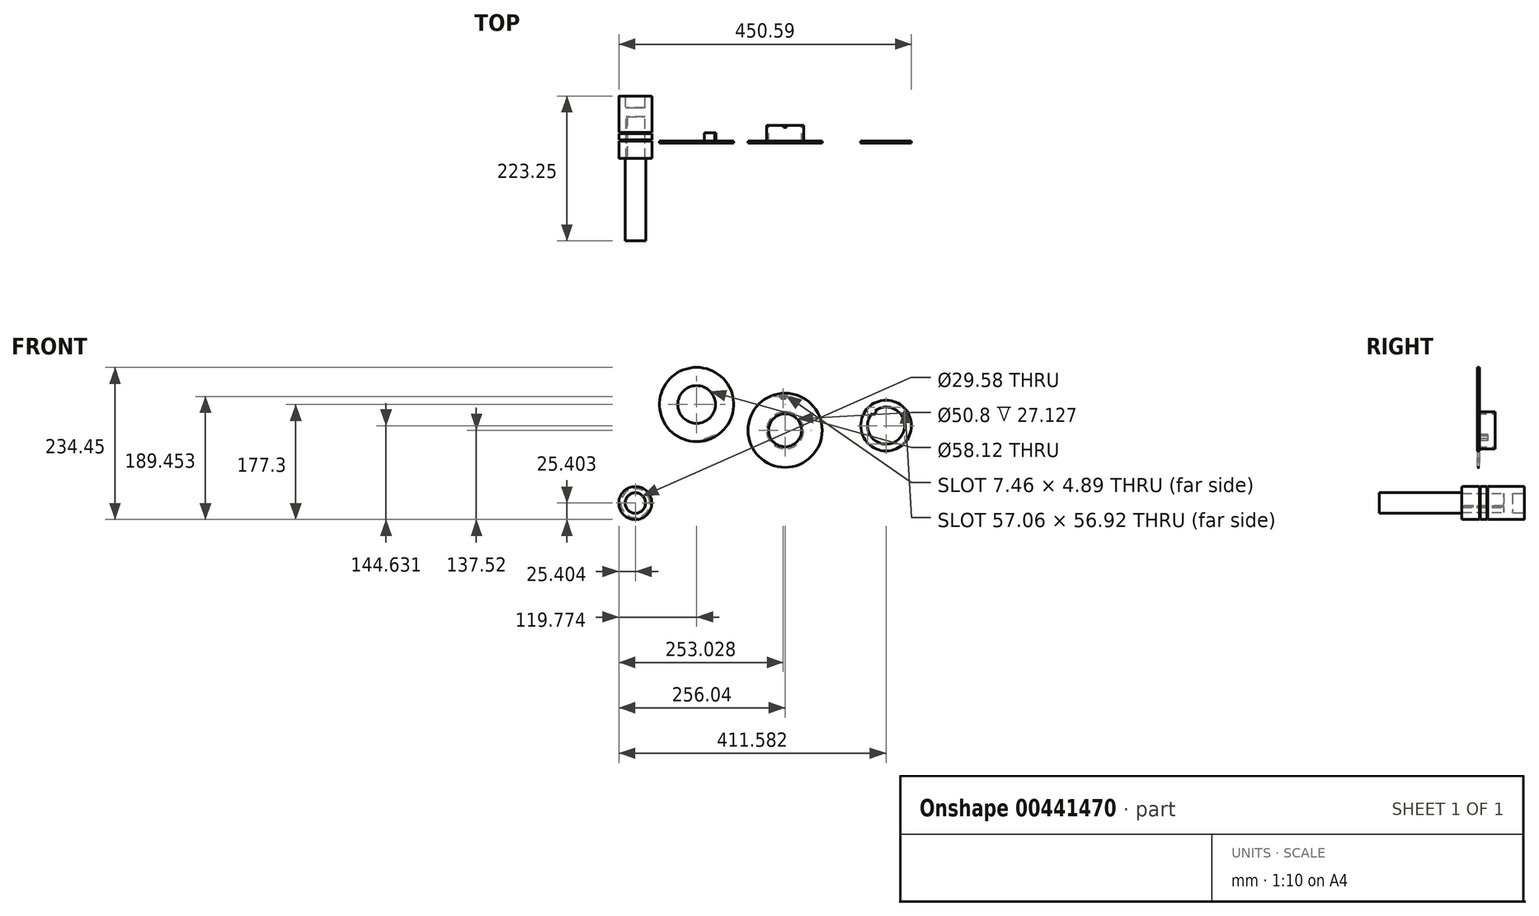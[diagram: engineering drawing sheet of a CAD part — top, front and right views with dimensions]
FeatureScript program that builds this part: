
annotation { "Feature Type Name" : "Feature", "Feature Type Description" : "" }
export const myFeature = defineFeature(function(context is Context, id is Id, definition is map)
    precondition{}
    {
        {
            var Q0;
            Q0=qCreatedBy(makeId("Front.planeOp"),FACE);
            var sketch = newSketch(context, id + "F0", { "sketchPlane" : qUnion([Q0])});
            skCircle(sketch, "E0", {"center": v(0, 0) * mm, "radius": 57.15 * mm});
            skCircle(sketch, "E1", {"center": v(0, 0) * mm, "radius": 25.4 * mm});
            skSolve(sketch);
        }
        {
            var Q0;
            Q0=makeQuery(id+"F0.imprint","IMPRINT",FACE,{"disambiguationData":[TD([[makeQuery(id+"F0.imprint","IMPRINT",EDGE,{"derivedFrom":sQuery(id+"F0.wireOp",EDGE,"E0")}),1.0]])]});
            extrude(context, id + "F1", {"entities" : qUnion([Q0]), "depth" : 3.17 * mm});
        }
        {
            var Q0;
            Q0=makeQuery(id+"F1.opExtrude","CAP_FACE",FACE,{"disambiguationData":[OSD([sQuery(id+"F0.wireOp",EDGE,"E0"),sQuery(id+"F0.wireOp",EDGE,"E1")])],"isStart":false});
            var sketch = newSketch(context, id + "F2", { "sketchPlane" : qUnion([Q0])});
            skLineSegment(sketch, "E2", {"start": v(0.72, 54.09) * mm, "end": v(0.72, 49.8) * mm});
            skLineSegment(sketch, "E3", {"start": v(-6.74, 49.9) * mm, "end": v(-6.62, 54.2) * mm});
            skArc(sketch, "E4", {"start": v(0.72, 54.09) * mm, "mid": v(-2.95, 54.38) * mm, "end": v(-6.62, 54.2) * mm});
            skArc(sketch, "E5", {"start": v(-6.74, 49.9) * mm, "mid": v(-3.02, 49.49) * mm, "end": v(0.72, 49.8) * mm});
            skSolve(sketch);
        }
        {
            var Q0;
            Q0=makeQuery(id+"F2.imprint","IMPRINT",FACE,{"disambiguationData":[TD([[makeQuery(id+"F2.imprint","IMPRINT",EDGE,{"derivedFrom":sQuery(id+"F2.wireOp",EDGE,"E2")}),-1.0]])]});
            extrude(context, id + "F3", {"entities" : qUnion([Q0]), "operationType" : NewBodyOperationType.REMOVE, "oppositeDirection" : true, "depth" : 25.4 * mm});
        }
        {
            var Q0;
            Q0=makeQuery(id+"F1.opExtrude","CAP_FACE",FACE,{"disambiguationData":[OSD([sQuery(id+"F0.wireOp",EDGE,"E0"),sQuery(id+"F0.wireOp",EDGE,"E1")])],"isStart":true});
            var sketch = newSketch(context, id + "F4", { "sketchPlane" : qUnion([Q0])});
            skCircle(sketch, "E6.0", {"center": v(0, 0) * mm, "radius": 25.4 * mm});
            skCircle(sketch, "E7", {"center": v(0, 0) * mm, "radius": 28.58 * mm});
            skSolve(sketch);
        }
        {
            var Q0;
            Q0=makeQuery(id+"F4.imprint","IMPRINT",FACE,{"disambiguationData":[TD([[makeQuery(id+"F4.imprint","IMPRINT",EDGE,{"derivedFrom":sQuery(id+"F4.wireOp",EDGE,"E6.0")}),1.0]])]});
            extrude(context, id + "F5", {"entities" : qUnion([Q0]), "operationType" : NewBodyOperationType.ADD, "depth" : 23.95 * mm});
        }
        {
            var Q0;
            Q0=qCreatedBy(makeId("Top.planeOp"),FACE);
            cPlane(context, id + "F6", {"entities" : qUnion([Q0]), "cplaneType" : CPlaneType.OFFSET, "offset" : 29.72 * mm, "width" : 152.4 * mm, "height" : 152.4 * mm});
        }
        {
            var Q0;
            Q0=qCreatedBy(id+"F6.planeOp",FACE);
            var sketch = newSketch(context, id + "F7", { "sketchPlane" : qUnion([Q0])});
            skLineSegment(sketch, "E8.bottom", {"start": v(-2.43, 24) * mm, "end": v(2.26, 24) * mm});
            skLineSegment(sketch, "E8.top", {"start": v(-2.43, 20.4) * mm, "end": v(2.26, 20.4) * mm});
            skLineSegment(sketch, "E8.left", {"start": v(-2.43, 24) * mm, "end": v(-2.43, 20.4) * mm});
            skLineSegment(sketch, "E8.right", {"start": v(2.26, 24) * mm, "end": v(2.26, 20.4) * mm});
            skSolve(sketch);
        }
        {
            var Q0;
            Q0 = qSketchRegion(id + "F7", true);
            extrude(context, id + "F8", {"entities" : qUnion([Q0]), "operationType" : NewBodyOperationType.REMOVE, "oppositeDirection" : true, "depth" : 25.4 * mm});
        }
        {
            var Q0;
            Q0=qCreatedBy(makeId("Front.planeOp"),FACE);
            var sketch = newSketch(context, id + "F9", { "sketchPlane" : qUnion([Q0])});
            skCircle(sketch, "E9", {"center": v(-136.27, 39.78) * mm, "radius": 57.15 * mm});
            skCircle(sketch, "E10", {"center": v(-136.27, 39.78) * mm, "radius": 29.06 * mm});
            skSolve(sketch);
        }
        {
            var Q0;
            Q0=makeQuery(id+"F9.imprint","IMPRINT",FACE,{"disambiguationData":[TD([[makeQuery(id+"F9.imprint","IMPRINT",EDGE,{"derivedFrom":sQuery(id+"F9.wireOp",EDGE,"E9")}),1.0]])]});
            extrude(context, id + "F10", {"entities" : qUnion([Q0]), "depth" : 3.17 * mm});
        }
        {
            var Q0;
            Q0=makeQuery(id+"F10.opExtrude","CAP_FACE",FACE,{"disambiguationData":[OSD([sQuery(id+"F9.wireOp",EDGE,"E9"),sQuery(id+"F9.wireOp",EDGE,"E10")])],"isStart":true});
            var sketch = newSketch(context, id + "F11", { "sketchPlane" : qUnion([Q0])});
            skPoint(sketch, "E11", {"position": v(123.88, -16.01) * mm});
            skPoint(sketch, "E12", {"position": v(106.52, -9.02) * mm});
            skArc(sketch, "E13", {"start": v(106.52, -9.02) * mm, "mid": v(114.92, -13.2) * mm, "end": v(123.88, -16.01) * mm});
            skArc(sketch, "E14.0", {"start": v(108.2, -6.23) * mm, "mid": v(116.14, -10.2) * mm, "end": v(124.6, -12.84) * mm});
            skLineSegment(sketch, "E15", {"start": v(123.88, -16.01) * mm, "end": v(124.6, -12.84) * mm});
            skLineSegment(sketch, "E16", {"start": v(106.52, -9.02) * mm, "end": v(108.2, -6.23) * mm});
            skSolve(sketch);
        }
        {
            var Q0;
            Q0=makeQuery(id+"F11.imprint","IMPRINT",FACE,{"disambiguationData":[TD([[makeQuery(id+"F11.imprint","IMPRINT",EDGE,{"derivedFrom":sQuery(id+"F11.wireOp",EDGE,"E13")}),1.0]])]});
            extrude(context, id + "F12", {"entities" : qUnion([Q0]), "operationType" : NewBodyOperationType.ADD, "depth" : 12.66 * mm});
        }
        {
            var Q0;
            Q0=qCreatedBy(makeId("Front.planeOp"),FACE);
            var sketch = newSketch(context, id + "F13", { "sketchPlane" : qUnion([Q0])});
            skCircle(sketch, "E17", {"center": v(-230.64, -112.12) * mm, "radius": 25.4 * mm});
            skSolve(sketch);
        }
        {
            var Q0;
            Q0=makeQuery(id+"F13.imprint","IMPRINT",FACE,{"disambiguationData":[TD([[makeQuery(id+"F13.imprint","IMPRINT",EDGE,{"derivedFrom":sQuery(id+"F13.wireOp",EDGE,"E17")}),1.0]])]});
            extrude(context, id + "F14", {"entities" : qUnion([Q0]), "depth" : 26.99 * mm});
        }
        {
            var Q0;
            Q0=makeQuery(id+"F14.opExtrude","CAP_FACE",FACE,{"disambiguationData":[OSD([sQuery(id+"F13.wireOp",EDGE,"E17")])],"isStart":true});
            var sketch = newSketch(context, id + "F15", { "sketchPlane" : qUnion([Q0])});
            skCircle(sketch, "E18", {"center": v(230.64, -112.12) * mm, "radius": 22.23 * mm});
            skSolve(sketch);
        }
        {
            var Q0;
            Q0=makeQuery(id+"F15.imprint","IMPRINT",FACE,{"disambiguationData":[TD([[makeQuery(id+"F15.imprint","IMPRINT",EDGE,{"derivedFrom":sQuery(id+"F15.wireOp",EDGE,"E18")}),1.0]])]});
            extrude(context, id + "F16", {"entities" : qUnion([Q0]), "operationType" : NewBodyOperationType.ADD, "depth" : 1.73 * mm});
        }
        {
            var Q0;
            Q0=makeQuery(id+"F16.opExtrude","CAP_FACE",FACE,{"disambiguationData":[OSD([sQuery(id+"F15.wireOp",EDGE,"E18")])],"isStart":false});
            var sketch = newSketch(context, id + "F17", { "sketchPlane" : qUnion([Q0])});
            skCircle(sketch, "E19.0", {"center": v(230.64, -112.12) * mm, "radius": 25.4 * mm});
            skSolve(sketch);
        }
        {
            var Q0;
            Q0=makeQuery(id+"F17.imprint","IMPRINT",FACE,{"disambiguationData":[TD([[makeQuery(id+"F17.imprint","IMPRINT",EDGE,{"derivedFrom":makeQuery(id+"F16.opExtrude","CAP_EDGE",EDGE,{"disambiguationData":[OSD([sQuery(id+"F15.wireOp",EDGE,"E18")])],"isStart":false})}),1.0]])]});
            var Q1;
            Q1=makeQuery(id+"F17.imprint","IMPRINT",FACE,{"disambiguationData":[TD([[makeQuery(id+"F17.imprint","IMPRINT",EDGE,{"derivedFrom":sQuery(id+"F17.wireOp",EDGE,"E19.0")}),1.0]])]});
            extrude(context, id + "F18", {"entities" : qUnion([Q0, Q1]), "operationType" : NewBodyOperationType.ADD, "depth" : 9.52 * mm});
        }
        {
            var Q0;
            Q0=makeQuery(id+"F18.opExtrude","CAP_FACE",FACE,{"disambiguationData":[OSD([sQuery(id+"F17.wireOp",EDGE,"E19.0")])],"isStart":false});
            var sketch = newSketch(context, id + "F19", { "sketchPlane" : qUnion([Q0])});
            skCircle(sketch, "E20", {"center": v(230.64, -112.12) * mm, "radius": 22.23 * mm});
            skSolve(sketch);
        }
        {
            var Q0;
            Q0=makeQuery(id+"F19.imprint","IMPRINT",FACE,{"disambiguationData":[TD([[makeQuery(id+"F19.imprint","IMPRINT",EDGE,{"derivedFrom":sQuery(id+"F19.wireOp",EDGE,"E20")}),1.0]])]});
            extrude(context, id + "F20", {"entities" : qUnion([Q0]), "operationType" : NewBodyOperationType.ADD, "depth" : 1.73 * mm});
        }
        {
            var Q0;
            Q0=makeQuery(id+"F20.opExtrude","CAP_FACE",FACE,{"disambiguationData":[OSD([sQuery(id+"F19.wireOp",EDGE,"E20")])],"isStart":false});
            var sketch = newSketch(context, id + "F21", { "sketchPlane" : qUnion([Q0])});
            skCircle(sketch, "E21.0", {"center": v(230.64, -112.12) * mm, "radius": 25.4 * mm});
            skSolve(sketch);
        }
        {
            var Q0;
            Q0=makeQuery(id+"F21.imprint","IMPRINT",FACE,{"disambiguationData":[TD([[makeQuery(id+"F21.imprint","IMPRINT",EDGE,{"derivedFrom":makeQuery(id+"F20.opExtrude","CAP_EDGE",EDGE,{"disambiguationData":[OSD([sQuery(id+"F19.wireOp",EDGE,"E20")])],"isStart":false})}),1.0]])]});
            var Q1;
            Q1=makeQuery(id+"F21.imprint","IMPRINT",FACE,{"disambiguationData":[TD([[makeQuery(id+"F21.imprint","IMPRINT",EDGE,{"derivedFrom":sQuery(id+"F21.wireOp",EDGE,"E21.0")}),1.0]])]});
            extrude(context, id + "F22", {"entities" : qUnion([Q0, Q1]), "operationType" : NewBodyOperationType.ADD, "depth" : 56.28 * mm});
        }
        {
            var Q0;
            Q0=makeQuery(id+"F22.opExtrude","CAP_FACE",FACE,{"disambiguationData":[OSD([sQuery(id+"F21.wireOp",EDGE,"E21.0")])],"isStart":false});
            var sketch = newSketch(context, id + "F23", { "sketchPlane" : qUnion([Q0])});
            skCircle(sketch, "E22", {"center": v(230.64, -112.12) * mm, "radius": 14.79 * mm});
            skSolve(sketch);
        }
        {
            var Q0;
            Q0=makeQuery(id+"F23.imprint","IMPRINT",FACE,{"disambiguationData":[TD([[makeQuery(id+"F23.imprint","IMPRINT",EDGE,{"derivedFrom":sQuery(id+"F23.wireOp",EDGE,"E22")}),1.0]])]});
            extrude(context, id + "F24", {"entities" : qUnion([Q0]), "operationType" : NewBodyOperationType.REMOVE, "oppositeDirection" : true, "depth" : 18.4 * mm});
        }
        {
            var Q0;
            Q0=makeQuery(id+"F14.opExtrude","CAP_FACE",FACE,{"disambiguationData":[OSD([sQuery(id+"F13.wireOp",EDGE,"E17")])],"isStart":false});
            var sketch = newSketch(context, id + "F25", { "sketchPlane" : qUnion([Q0])});
            skCircle(sketch, "E23", {"center": v(-230.64, -112.12) * mm, "radius": 15.88 * mm});
            skSolve(sketch);
        }
        {
            var Q0;
            Q0=makeQuery(id+"F25.imprint","IMPRINT",FACE,{"disambiguationData":[TD([[makeQuery(id+"F25.imprint","IMPRINT",EDGE,{"derivedFrom":sQuery(id+"F25.wireOp",EDGE,"E23")}),1.0]])]});
            extrude(context, id + "F26", {"entities" : qUnion([Q0]), "operationType" : NewBodyOperationType.REMOVE, "oppositeDirection" : true, "depth" : 64.36 * mm});
        }
        {
            var Q0;
            Q0=makeQuery(id+"F22.opExtrude","CAP_EDGE",EDGE,{"disambiguationData":[OSD([sQuery(id+"F21.wireOp",EDGE,"E21.0")])],"isStart":false});
            var Q1;
            Q1=makeQuery(id+"F14.opExtrude","CAP_EDGE",EDGE,{"disambiguationData":[OSD([sQuery(id+"F13.wireOp",EDGE,"E17")])],"isStart":false});
            var Q2;
            Q2=makeQuery(id+"F24.boolean.opBoolean","COPY",FACE,{"derivedFrom":makeQuery(id+"F24.opExtrude","CAP_FACE",FACE,{"disambiguationData":[OSD([sQuery(id+"F23.wireOp",EDGE,"E22")])],"isStart":false})});
            var Q3;
            Q3=makeQuery(id+"F24.boolean.opBoolean","COPY",EDGE,{"derivedFrom":makeQuery(id+"F24.opExtrude","CAP_EDGE",EDGE,{"disambiguationData":[OSD([sQuery(id+"F23.wireOp",EDGE,"E22")])],"isStart":true})});
            fillet(context, id + "F27", {"entities" : qUnion([Q0, Q1, Q2, Q3]), "radius" : 1.27 * mm, "tangentPropagation" : true, "allowEdgeOverflow" : false});
        }
        {
            var Q0;
            Q0=makeQuery(id+"F26.boolean.opBoolean","COPY",EDGE,{"derivedFrom":makeQuery(id+"F26.opExtrude","CAP_EDGE",EDGE,{"disambiguationData":[OSD([sQuery(id+"F25.wireOp",EDGE,"E23")])],"isStart":false})});
            chamfer(context, id + "F28", {"entities" : qUnion([Q0]), "width" : 1.27 * mm, "tangentPropagation" : true});
        }
        {
            var Q0;
            Q0=makeQuery(id+"F14.opExtrude","CAP_FACE",FACE,{"disambiguationData":[OSD([sQuery(id+"F13.wireOp",EDGE,"E17")])],"isStart":false});
            var sketch = newSketch(context, id + "F29", { "sketchPlane" : qUnion([Q0])});
            skLineSegment(sketch, "E24", {"start": v(-245.74, -116.99) * mm, "end": v(-243.82, -116.26) * mm});
            skLineSegment(sketch, "E25", {"start": v(-242.98, -118.5) * mm, "end": v(-244.84, -119.2) * mm});
            skArc(sketch, "E26", {"start": v(-242.98, -118.5) * mm, "mid": v(-243.39, -117.37) * mm, "end": v(-243.82, -116.26) * mm});
            skArc(sketch, "E27", {"start": v(-245.74, -116.99) * mm, "mid": v(-245.34, -118.12) * mm, "end": v(-244.84, -119.2) * mm});
            skSolve(sketch);
        }
        {
            var Q0;
            Q0=makeQuery(id+"F29.imprint","IMPRINT",FACE,{"disambiguationData":[TD([[makeQuery(id+"F29.imprint","IMPRINT",EDGE,{"derivedFrom":sQuery(id+"F29.wireOp",EDGE,"E24")}),-1.0]])]});
            var Q1;
            Q1=makeQuery(id+"F26.boolean.opBoolean","COPY",FACE,{"derivedFrom":makeQuery(id+"F26.opExtrude","CAP_FACE",FACE,{"disambiguationData":[OSD([sQuery(id+"F25.wireOp",EDGE,"E23")])],"isStart":false})});
            extrude(context, id + "F30", {"entities" : qUnion([Q0]), "operationType" : NewBodyOperationType.ADD, "endBound" : BoundingType.UP_TO_SURFACE, "oppositeDirection" : true, "endBoundEntityFace" : qUnion([Q1]), "depth" : 25.4 * mm});
        }
        {
            var Q0;
            Q0=makeQuery(id+"F30.opExtrude","CAP_EDGE",EDGE,{"disambiguationData":[OSD([sQuery(id+"F29.wireOp",EDGE,"E26")])],"isStart":true});
            chamfer(context, id + "F31", {"entities" : qUnion([Q0]), "width" : 1.99 * mm, "tangentPropagation" : true});
        }
        {
            var Q0;
            Q0=qCreatedBy(makeId("Front.planeOp"),FACE);
            var sketch = newSketch(context, id + "F32", { "sketchPlane" : qUnion([Q0])});
            skCircle(sketch, "E28", {"center": v(155.57, 7.22) * mm, "radius": 38.99 * mm});
            skCircle(sketch, "E29", {"center": v(155.57, 7.22) * mm, "radius": 28.58 * mm});
            skLineSegment(sketch, "E30", {"start": v(138.7, 30.29) * mm, "end": v(140.88, 27.95) * mm});
            skLineSegment(sketch, "E31", {"start": v(134.02, 26) * mm, "end": v(136.2, 23.66) * mm});
            skArc(sketch, "E32", {"start": v(140.88, 27.95) * mm, "mid": v(138.34, 26.03) * mm, "end": v(136.2, 23.66) * mm});
            skSolve(sketch);
        }
        {
            var Q0;
            Q0 = qSketchRegion(id + "F32", true);
            var Q1;
            {var subQ0=sQuery(id+"F32.wireOp",EDGE,"E30");Q1=makeQuery(id+"F32.imprint","IMPRINT",FACE,{"disambiguationData":[TD([[makeQuery(id+"F32.imprint","IMPRINT",EDGE,{"derivedFrom":subQ0}),-1.0]])]});}
            extrude(context, id + "F33", {"entities" : qUnion([Q0, Q1]), "depth" : 3.17 * mm});
        }
        {
            var Q0;
            Q0=qCreatedBy(makeId("Front.planeOp"),FACE);
            var sketch = newSketch(context, id + "F34", { "sketchPlane" : qUnion([Q0])});
            skCircle(sketch, "E33", {"center": v(271, -56.7) * mm, "radius": 55.3 * mm});
            skSolve(sketch);
        }
        {
            var Q0;
            Q0=makeQuery(id+"F34.imprint","IMPRINT",FACE,{"disambiguationData":[TD([[makeQuery(id+"F34.imprint","IMPRINT",EDGE,{"derivedFrom":sQuery(id+"F34.wireOp",EDGE,"E33")}),1.0]])]});
            extrude(context, id + "F35", {"entities" : qUnion([Q0]), "depth" : 174.5 * mm});
        }
        {
            var Q0;
            Q0=makeQuery(id+"F35.opExtrude","SWEPT_BODY",BODY,{"disambiguationData":[OSD([sQuery(id+"F34.wireOp",EDGE,"E33")])]});
            deleteBodies(context, id + "F36", {"entities" : qUnion([Q0])});
        }
        {
            var Q0;
            Q0=makeQuery(id+"F26.boolean.opBoolean","COPY",FACE,{"derivedFrom":makeQuery(id+"F26.opExtrude","CAP_FACE",FACE,{"disambiguationData":[OSD([sQuery(id+"F25.wireOp",EDGE,"E23")])],"isStart":false})});
            var sketch = newSketch(context, id + "F37", { "sketchPlane" : qUnion([Q0])});
            skCircle(sketch, "E34.0", {"center": v(-230.64, -112.12) * mm, "radius": 24.13 * mm});
            skCircle(sketch, "E35", {"center": v(-230.64, -112.12) * mm, "radius": 15.88 * mm});
            skSolve(sketch);
        }
        {
            var Q0;
            Q0=makeQuery(id+"F37.imprint","IMPRINT",FACE,{"disambiguationData":[TD([[makeQuery(id+"F37.imprint","IMPRINT",EDGE,{"derivedFrom":sQuery(id+"F37.wireOp",EDGE,"E35")}),1.0]])]});
            var Q1;
            {var subQ0=sQuery(id+"F25.wireOp",EDGE,"E23");var subQ1=makeQuery(id+"F26.boolean.opBoolean","COPY",FACE,{"derivedFrom":makeQuery(id+"F26.opExtrude","CAP_FACE",FACE,{"disambiguationData":[OSD([subQ0])],"isStart":false})});var subQ2=subQ1;var subQ17=sQuery(id+"F29.wireOp",EDGE,"E24");var subQ18=makeQuery(id+"F29.imprint","IMPRINT",EDGE,{"derivedFrom":subQ17});Q1=makeQuery(id+"F37.imprint","IMPRINT",FACE,{"disambiguationData":[TD([[makeQuery(id+"F37.imprint","IMPRINT",EDGE,{"derivedFrom":makeQuery(id+"F30.opExtrude","TWEAK_EDGE",EDGE,{"derivedFrom":[subQ2,subQ18]})}),-1.0]])]});}
            var Q2;
            {var subQ0=sQuery(id+"F29.wireOp",EDGE,"E26");var subQ1=sQuery(id+"F29.wireOp",EDGE,"E25");var subQ2=sQuery(id+"F29.wireOp",EDGE,"E24");var subQ3=sQuery(id+"F25.wireOp",EDGE,"E23");Q2=makeQuery(id+"FPU4hDJRsUAHc8M_3.17.F30.boolean.opBoolean","MERGE",FACE,{"derivedFrom":[makeQuery(id+"FPU4hDJRsUAHc8M_3.16.F30.boolean.opBoolean","MERGE",FACE,{"derivedFrom":[makeQuery(id+"FPU4hDJRsUAHc8M_3.15.F30.boolean.opBoolean","MERGE",FACE,{"derivedFrom":[makeQuery(id+"FPU4hDJRsUAHc8M_3.14.F30.boolean.opBoolean","MERGE",FACE,{"derivedFrom":[makeQuery(id+"FPU4hDJRsUAHc8M_3.13.F30.boolean.opBoolean","MERGE",FACE,{"derivedFrom":[makeQuery(id+"FPU4hDJRsUAHc8M_3.12.F30.boolean.opBoolean","MERGE",FACE,{"derivedFrom":[makeQuery(id+"FPU4hDJRsUAHc8M_3.11.F30.boolean.opBoolean","MERGE",FACE,{"derivedFrom":[makeQuery(id+"FPU4hDJRsUAHc8M_3.10.F30.boolean.opBoolean","MERGE",FACE,{"derivedFrom":[makeQuery(id+"FPU4hDJRsUAHc8M_3.9.F30.boolean.opBoolean","MERGE",FACE,{"derivedFrom":[makeQuery(id+"FPU4hDJRsUAHc8M_3.8.F30.boolean.opBoolean","MERGE",FACE,{"derivedFrom":[makeQuery(id+"FPU4hDJRsUAHc8M_3.7.F30.boolean.opBoolean","MERGE",FACE,{"derivedFrom":[makeQuery(id+"FPU4hDJRsUAHc8M_3.6.F30.boolean.opBoolean","MERGE",FACE,{"derivedFrom":[makeQuery(id+"FPU4hDJRsUAHc8M_3.5.F30.boolean.opBoolean","MERGE",FACE,{"derivedFrom":[makeQuery(id+"FPU4hDJRsUAHc8M_3.4.F30.boolean.opBoolean","MERGE",FACE,{"derivedFrom":[makeQuery(id+"FPU4hDJRsUAHc8M_3.3.F30.boolean.opBoolean","MERGE",FACE,{"derivedFrom":[makeQuery(id+"FPU4hDJRsUAHc8M_3.2.F30.boolean.opBoolean","MERGE",FACE,{"derivedFrom":[makeQuery(id+"FPU4hDJRsUAHc8M_3.1.F30.boolean.opBoolean","MERGE",FACE,{"derivedFrom":[makeQuery(id+"F30.boolean.opBoolean","MERGE",FACE,{"derivedFrom":[makeQuery(id+"F14.opExtrude","CAP_FACE",FACE,{"disambiguationData":[OSD([sQuery(id+"F13.wireOp",EDGE,"E17")])],"isStart":false}),makeQuery(id+"F30.opExtrude","CAP_FACE",FACE,{"disambiguationData":[OSD([subQ3,subQ2,subQ1,subQ0])],"isStart":true})]}),makeQuery(id+"FPU4hDJRsUAHc8M_3.1.F30.opExtrude","CAP_FACE",FACE,{"disambiguationData":[OSD([subQ3,subQ2,subQ1,subQ0])],"isStart":true})]}),makeQuery(id+"FPU4hDJRsUAHc8M_3.2.F30.opExtrude","CAP_FACE",FACE,{"disambiguationData":[OSD([subQ3,subQ2,subQ1,subQ0])],"isStart":true})]}),makeQuery(id+"FPU4hDJRsUAHc8M_3.3.F30.opExtrude","CAP_FACE",FACE,{"disambiguationData":[OSD([subQ3,subQ2,subQ1,subQ0])],"isStart":true})]}),makeQuery(id+"FPU4hDJRsUAHc8M_3.4.F30.opExtrude","CAP_FACE",FACE,{"disambiguationData":[OSD([subQ3,subQ2,subQ1,subQ0])],"isStart":true})]}),makeQuery(id+"FPU4hDJRsUAHc8M_3.5.F30.opExtrude","CAP_FACE",FACE,{"disambiguationData":[OSD([subQ3,subQ2,subQ1,subQ0])],"isStart":true})]}),makeQuery(id+"FPU4hDJRsUAHc8M_3.6.F30.opExtrude","CAP_FACE",FACE,{"disambiguationData":[OSD([subQ3,subQ2,subQ1,subQ0])],"isStart":true})]}),makeQuery(id+"FPU4hDJRsUAHc8M_3.7.F30.opExtrude","CAP_FACE",FACE,{"disambiguationData":[OSD([subQ3,subQ2,subQ1,subQ0])],"isStart":true})]}),makeQuery(id+"FPU4hDJRsUAHc8M_3.8.F30.opExtrude","CAP_FACE",FACE,{"disambiguationData":[OSD([subQ3,subQ2,subQ1,subQ0])],"isStart":true})]}),makeQuery(id+"FPU4hDJRsUAHc8M_3.9.F30.opExtrude","CAP_FACE",FACE,{"disambiguationData":[OSD([subQ3,subQ2,subQ1,subQ0])],"isStart":true})]}),makeQuery(id+"FPU4hDJRsUAHc8M_3.10.F30.opExtrude","CAP_FACE",FACE,{"disambiguationData":[OSD([subQ3,subQ2,subQ1,subQ0])],"isStart":true})]}),makeQuery(id+"FPU4hDJRsUAHc8M_3.11.F30.opExtrude","CAP_FACE",FACE,{"disambiguationData":[OSD([subQ3,subQ2,subQ1,subQ0])],"isStart":true})]}),makeQuery(id+"FPU4hDJRsUAHc8M_3.12.F30.opExtrude","CAP_FACE",FACE,{"disambiguationData":[OSD([subQ3,subQ2,subQ1,subQ0])],"isStart":true})]}),makeQuery(id+"FPU4hDJRsUAHc8M_3.13.F30.opExtrude","CAP_FACE",FACE,{"disambiguationData":[OSD([subQ3,subQ2,subQ1,subQ0])],"isStart":true})]}),makeQuery(id+"FPU4hDJRsUAHc8M_3.14.F30.opExtrude","CAP_FACE",FACE,{"disambiguationData":[OSD([subQ3,subQ2,subQ1,subQ0])],"isStart":true})]}),makeQuery(id+"FPU4hDJRsUAHc8M_3.15.F30.opExtrude","CAP_FACE",FACE,{"disambiguationData":[OSD([subQ3,subQ2,subQ1,subQ0])],"isStart":true})]}),makeQuery(id+"FPU4hDJRsUAHc8M_3.16.F30.opExtrude","CAP_FACE",FACE,{"disambiguationData":[OSD([subQ3,subQ2,subQ1,subQ0])],"isStart":true})]}),makeQuery(id+"FPU4hDJRsUAHc8M_3.17.F30.opExtrude","CAP_FACE",FACE,{"disambiguationData":[OSD([subQ3,subQ2,subQ1,subQ0])],"isStart":true})]});}
            extrude(context, id + "F38", {"entities" : qUnion([Q0, Q1]), "endBound" : BoundingType.UP_TO_SURFACE, "endBoundEntityFace" : qUnion([Q2]), "depth" : 76.2 * mm});
        }
        {
            var Q0;
            Q0=makeQuery(id+"F14.opExtrude","SWEPT_BODY",BODY,{"disambiguationData":[OSD([sQuery(id+"F13.wireOp",EDGE,"E17")])]});
            var Q1;
            Q1=makeQuery(id+"F38.opExtrude","SWEPT_BODY",BODY,{"disambiguationData":[OSD([sQuery(id+"F37.wireOp",EDGE,"E35")])]});
            booleanBodies(context, id + "F39", {"operationType" : BooleanOperationType.SUBTRACTION, "tools" : qUnion([Q0]), "targets" : qUnion([Q1]), "keepTools" : true});
        }
        {
            var Q0;
            Q0=makeQuery(id+"F38.opExtrude","CAP_FACE",FACE,{"disambiguationData":[OSD([sQuery(id+"F13.wireOp",EDGE,"E17"),sQuery(id+"F25.wireOp",EDGE,"E23"),sQuery(id+"F29.wireOp",EDGE,"E24"),sQuery(id+"F29.wireOp",EDGE,"E25"),sQuery(id+"F29.wireOp",EDGE,"E26")])],"isStart":false});
            var sketch = newSketch(context, id + "F40", { "sketchPlane" : qUnion([Q0])});
            skCircle(sketch, "E36", {"center": v(-230.64, -112.12) * mm, "radius": 15.87 * mm});
            skSolve(sketch);
        }
        {
            var Q0;
            Q0 = qSketchRegion(id + "F40", true);
            extrude(context, id + "F41", {"entities" : qUnion([Q0]), "operationType" : NewBodyOperationType.ADD, "depth" : 127 * mm});
        }
    });
